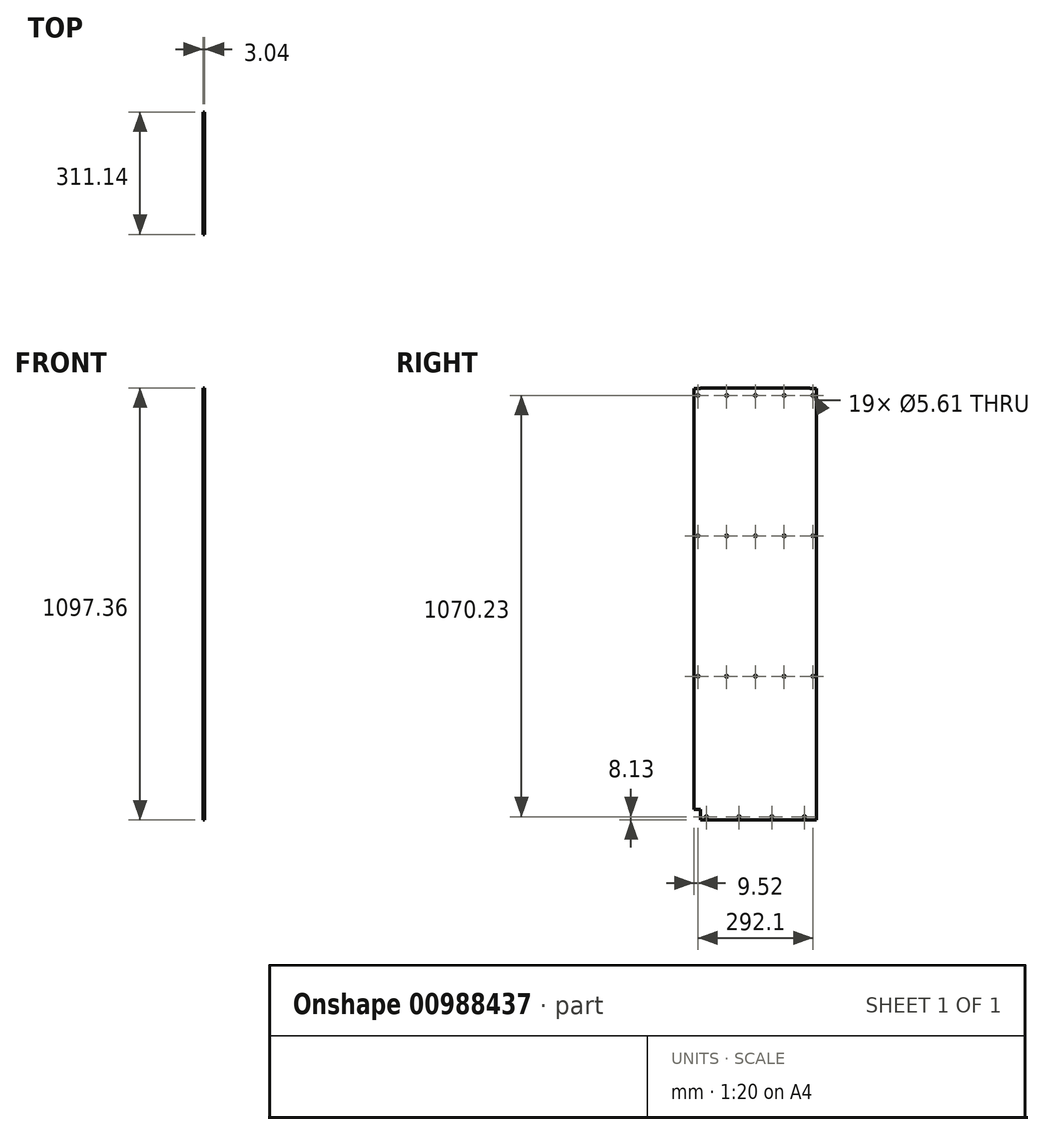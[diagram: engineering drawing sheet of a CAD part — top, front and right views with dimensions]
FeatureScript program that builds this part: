
annotation { "Feature Type Name" : "Feature", "Feature Type Description" : "" }
export const myFeature = defineFeature(function(context is Context, id is Id, definition is map)
    precondition{}
    {
        {
            var Q0;
            Q0=qCreatedBy(makeId("Right.planeOp"),FACE);
            var sketch = newSketch(context, id + "F0", { "sketchPlane" : qUnion([Q0])});
            skLineSegment(sketch, "E0.bottom", {"start": v(155.57, 548.68) * mm, "end": v(-155.58, 548.68) * mm});
            skLineSegment(sketch, "E0.top", {"start": v(155.58, -548.68) * mm, "end": v(-155.57, -548.68) * mm});
            skLineSegment(sketch, "E0.left", {"start": v(155.57, 548.68) * mm, "end": v(155.58, -548.68) * mm});
            skLineSegment(sketch, "E0.right", {"start": v(-155.58, 548.68) * mm, "end": v(-155.57, -548.68) * mm});
            skPoint(sketch, "E0.middle", {"position": v(0, 0) * mm});
            skSolve(sketch);
        }
        {
            var Q0;
            Q0 = qSketchRegion(id + "F0", true);
            extrude(context, id + "F1", {"entities" : qUnion([Q0]), "depth" : 3.04 * mm, "offsetDistance" : 25.4 * mm, "symmetric" : true});
        }
        {
            var Q0;
            Q0=makeQuery(id+"F1.opExtrude","CAP_FACE",FACE,{"disambiguationData":[OSD([sQuery(id+"F0.wireOp",EDGE,"E0.bottom"),sQuery(id+"F0.wireOp",EDGE,"E0.top"),sQuery(id+"F0.wireOp",EDGE,"E0.left"),sQuery(id+"F0.wireOp",EDGE,"E0.right")])],"isStart":false});
            var sketch = newSketch(context, id + "F2", { "sketchPlane" : qUnion([Q0])});
            skLineSegment(sketch, "E1.bottom", {"start": v(-155.57, -548.68) * mm, "end": v(-139.06, -548.68) * mm});
            skLineSegment(sketch, "E1.top", {"start": v(-155.57, -521.53) * mm, "end": v(-139.06, -521.53) * mm});
            skLineSegment(sketch, "E1.left", {"start": v(-155.57, -548.68) * mm, "end": v(-155.57, -521.53) * mm});
            skLineSegment(sketch, "E1.right", {"start": v(-139.06, -548.68) * mm, "end": v(-139.06, -521.53) * mm});
            skLineSegment(sketch, "E2", {"start": v(0, 548.68) * mm, "end": v(0, -548.68) * mm, "construction": true});
            skSolve(sketch);
        }
        {
            var Q0;
            Q0 = qSketchRegion(id + "F2", true);
            extrude(context, id + "F3", {"entities" : qUnion([Q0]), "operationType" : NewBodyOperationType.REMOVE, "endBound" : BoundingType.UP_TO_NEXT, "oppositeDirection" : true, "depth" : 25.4 * mm, "offsetDistance" : 25.4 * mm});
        }
        {
            var Q0;
            Q0=makeQuery(id+"F1.opExtrude","CAP_FACE",FACE,{"disambiguationData":[OSD([sQuery(id+"F0.wireOp",EDGE,"E0.bottom"),sQuery(id+"F0.wireOp",EDGE,"E0.top"),sQuery(id+"F0.wireOp",EDGE,"E0.left"),sQuery(id+"F0.wireOp",EDGE,"E0.right")])],"isStart":false});
            var sketch = newSketch(context, id + "F4", { "sketchPlane" : qUnion([Q0])});
            skLineSegment(sketch, "E3.bottom", {"start": v(-155.58, 548.68) * mm, "end": v(-139.06, 548.68) * mm});
            skLineSegment(sketch, "E3.top", {"start": v(-155.58, 546.77) * mm, "end": v(-139.06, 546.77) * mm});
            skLineSegment(sketch, "E3.left", {"start": v(-155.58, 548.68) * mm, "end": v(-155.58, 546.77) * mm});
            skLineSegment(sketch, "E3.right", {"start": v(-139.06, 548.68) * mm, "end": v(-139.06, 546.77) * mm});
            skLineSegment(sketch, "E4", {"start": v(-139.06, -521.53) * mm, "end": v(-139.06, 546.77) * mm, "construction": true});
            skLineSegment(sketch, "E5.MirrorCS", {"start": v(139.06, 548.68) * mm, "end": v(139.06, 546.77) * mm});
            skLineSegment(sketch, "E6.MirrorCS", {"start": v(155.58, 548.68) * mm, "end": v(155.58, 546.77) * mm});
            skLineSegment(sketch, "E7.MirrorCS", {"start": v(155.58, 546.77) * mm, "end": v(139.06, 546.77) * mm});
            skLineSegment(sketch, "E8.MirrorCS", {"start": v(155.58, 548.68) * mm, "end": v(139.06, 548.68) * mm});
            skSolve(sketch);
        }
        {
            var Q0;
            Q0 = qSketchRegion(id + "F4", true);
            extrude(context, id + "F5", {"entities" : qUnion([Q0]), "operationType" : NewBodyOperationType.REMOVE, "endBound" : BoundingType.UP_TO_NEXT, "oppositeDirection" : true, "depth" : 25.4 * mm, "offsetDistance" : 25.4 * mm});
        }
        {
            var Q0;
            Q0=makeQuery(id+"F1.opExtrude","CAP_FACE",FACE,{"disambiguationData":[OSD([sQuery(id+"F0.wireOp",EDGE,"E0.bottom"),sQuery(id+"F0.wireOp",EDGE,"E0.top"),sQuery(id+"F0.wireOp",EDGE,"E0.left"),sQuery(id+"F0.wireOp",EDGE,"E0.right")])],"isStart":true});
            var sketch = newSketch(context, id + "F6", { "sketchPlane" : qUnion([Q0])});
            skLineSegment(sketch, "E9", {"start": v(139.06, -540.55) * mm, "end": v(124.59, -540.55) * mm, "construction": true});
            skLineSegment(sketch, "E10", {"start": v(124.59, -540.55) * mm, "end": v(41.53, -540.55) * mm, "construction": true});
            skLineSegment(sketch, "E11", {"start": v(41.53, -540.55) * mm, "end": v(-41.53, -540.55) * mm, "construction": true});
            skLineSegment(sketch, "E12", {"start": v(-41.53, -540.55) * mm, "end": v(-124.59, -540.55) * mm, "construction": true});
            skLineSegment(sketch, "E13", {"start": v(-124.59, -540.55) * mm, "end": v(-139.06, -540.55) * mm, "construction": true});
            skLineSegment(sketch, "E14", {"start": v(-146.05, -183.8) * mm, "end": v(-73.03, -183.8) * mm, "construction": true});
            skLineSegment(sketch, "E15", {"start": v(-73.03, -183.8) * mm, "end": v(0, -183.8) * mm, "construction": true});
            skLineSegment(sketch, "E16", {"start": v(0, -183.8) * mm, "end": v(73.02, -183.8) * mm, "construction": true});
            skLineSegment(sketch, "E17", {"start": v(73.02, -183.8) * mm, "end": v(146.05, -183.8) * mm, "construction": true});
            skLineSegment(sketch, "E18", {"start": v(-146.05, -183.8) * mm, "end": v(-155.58, -183.8) * mm, "construction": true});
            skLineSegment(sketch, "E19", {"start": v(146.05, -183.8) * mm, "end": v(155.57, -183.8) * mm, "construction": true});
            skLineSegment(sketch, "E20", {"start": v(-146.05, -183.8) * mm, "end": v(-146.05, 172.94) * mm, "construction": true});
            skLineSegment(sketch, "E21", {"start": v(-146.05, 172.94) * mm, "end": v(-73.03, 172.94) * mm, "construction": true});
            skLineSegment(sketch, "E22", {"start": v(-73.03, 172.94) * mm, "end": v(0, 172.94) * mm, "construction": true});
            skLineSegment(sketch, "E23", {"start": v(0, 172.94) * mm, "end": v(73.02, 172.94) * mm, "construction": true});
            skLineSegment(sketch, "E24", {"start": v(73.02, 172.94) * mm, "end": v(146.05, 172.94) * mm, "construction": true});
            skLineSegment(sketch, "E25", {"start": v(146.05, 172.94) * mm, "end": v(146.05, -183.8) * mm, "construction": true});
            skLineSegment(sketch, "E26", {"start": v(146.05, 172.94) * mm, "end": v(146.05, 529.68) * mm, "construction": true});
            skLineSegment(sketch, "E27", {"start": v(146.05, 529.68) * mm, "end": v(73.03, 529.68) * mm, "construction": true});
            skLineSegment(sketch, "E28", {"start": v(73.03, 529.68) * mm, "end": v(0, 529.68) * mm, "construction": true});
            skLineSegment(sketch, "E29", {"start": v(0, 529.68) * mm, "end": v(-73.02, 529.68) * mm, "construction": true});
            skLineSegment(sketch, "E30", {"start": v(-73.02, 529.68) * mm, "end": v(-146.05, 529.68) * mm, "construction": true});
            skLineSegment(sketch, "E31", {"start": v(-146.05, 529.68) * mm, "end": v(-146.05, 172.94) * mm, "construction": true});
            skSolve(sketch);
        }
        {
            var Q0;
            Q0=sQuery(id+"F6.wireOp",VERTEX,"3fb6df0f-48ea-47ba-a382-073ea98ab63a.0.center");
            var Q1;
            Q1=sQuery(id+"F6.wireOp",VERTEX,"3fb6df0f-48ea-47ba-a382-073ea98ab63a.1.center");
            var Q2;
            Q2=sQuery(id+"F6.wireOp",VERTEX,"3fb6df0f-48ea-47ba-a382-073ea98ab63a.2.center");
            var Q3;
            Q3=sQuery(id+"F6.wireOp",VERTEX,"3fb6df0f-48ea-47ba-a382-073ea98ab63a.4.center");
            var Q4;
            Q4=sQuery(id+"F6.wireOp",VERTEX,"3fb6df0f-48ea-47ba-a382-073ea98ab63a.3.center");
            var Q5;
            Q5=sQuery(id+"F6.wireOp",VERTEX,"ec28871b-28f6-4f57-aad8-db33018dbeac.0.center");
            var Q6;
            Q6=sQuery(id+"F6.wireOp",VERTEX,"ec28871b-28f6-4f57-aad8-db33018dbeac.2.center");
            var Q7;
            Q7=sQuery(id+"F6.wireOp",VERTEX,"ec28871b-28f6-4f57-aad8-db33018dbeac.3.center");
            var Q8;
            Q8=sQuery(id+"F6.wireOp",VERTEX,"ec28871b-28f6-4f57-aad8-db33018dbeac.4.center");
            var Q9;
            Q9=sQuery(id+"F6.wireOp",VERTEX,"ec28871b-28f6-4f57-aad8-db33018dbeac.1.center");
            var Q10;
            Q10=sQuery(id+"F6.wireOp",VERTEX,"E9.end");
            var Q11;
            Q11=sQuery(id+"F6.wireOp",VERTEX,"E10.end");
            var Q12;
            Q12=sQuery(id+"F6.wireOp",VERTEX,"E11.end");
            var Q13;
            Q13=sQuery(id+"F6.wireOp",VERTEX,"E12.end");
            var Q14;
            Q14=sQuery(id+"F6.wireOp",VERTEX,"E17.end");
            var Q15;
            Q15=sQuery(id+"F6.wireOp",VERTEX,"E24.end");
            var Q16;
            Q16=sQuery(id+"F6.wireOp",VERTEX,"E23.end");
            var Q17;
            Q17=sQuery(id+"F6.wireOp",VERTEX,"E22.end");
            var Q18;
            Q18=sQuery(id+"F6.wireOp",VERTEX,"E21.end");
            var Q19;
            Q19=sQuery(id+"F6.wireOp",VERTEX,"E20.end");
            var Q20;
            Q20=sQuery(id+"F6.wireOp",VERTEX,"E14.start");
            var Q21;
            Q21=sQuery(id+"F6.wireOp",VERTEX,"E14.end");
            var Q22;
            Q22=sQuery(id+"F6.wireOp",VERTEX,"E15.end");
            var Q23;
            Q23=sQuery(id+"F6.wireOp",VERTEX,"E16.end");
            var Q24;
            Q24=sQuery(id+"F6.wireOp",VERTEX,"E26.end");
            var Q25;
            Q25=sQuery(id+"F6.wireOp",VERTEX,"E27.end");
            var Q26;
            Q26=sQuery(id+"F6.wireOp",VERTEX,"E28.end");
            var Q27;
            Q27=sQuery(id+"F6.wireOp",VERTEX,"E29.end");
            var Q28;
            Q28=sQuery(id+"F6.wireOp",VERTEX,"E30.end");
            var Q29;
            Q29=makeQuery(id+"F1.opExtrude","SWEPT_BODY",BODY,{"disambiguationData":[OSD([sQuery(id+"F0.wireOp",EDGE,"E0.bottom"),sQuery(id+"F0.wireOp",EDGE,"E0.top"),sQuery(id+"F0.wireOp",EDGE,"E0.left"),sQuery(id+"F0.wireOp",EDGE,"E0.right")])]});
            hole(context, id + "F7", {"style" : HoleStyle.SIMPLE, "endStyle" : HoleEndStyle.THROUGH, "standardTappedOrClearance" : lookupTablePath({ "fit" : "Normal (ASME)", "standard" : "ANSI", "size" : "#10", "type" : "Clearance" }), "standardBlindInLast" : lookupTablePath({ "fit" : "Normal", "standard" : "ANSI", "engagement" : "75%", "pitch" : "24 tpi", "size" : "#10", "type" : "Clearance & tapped" }), "holeDiameter" : 5.61 * mm, "majorDiameter" : 6.35 * mm, "isTappedThrough" : true, "tappedDepth" : 12.7 * mm, "tapClearance" : 3, "locations" : qUnion([Q0, Q1, Q2, Q3, Q4, Q5, Q6, Q7, Q8, Q9, Q10, Q11, Q12, Q13, Q14, Q15, Q16, Q17, Q18, Q19, Q20, Q21, Q22, Q23, Q24, Q25, Q26, Q27, Q28]), "scope" : qUnion([Q29]), "startStyle" : HoleStartStyle.PART});
        }
    });
